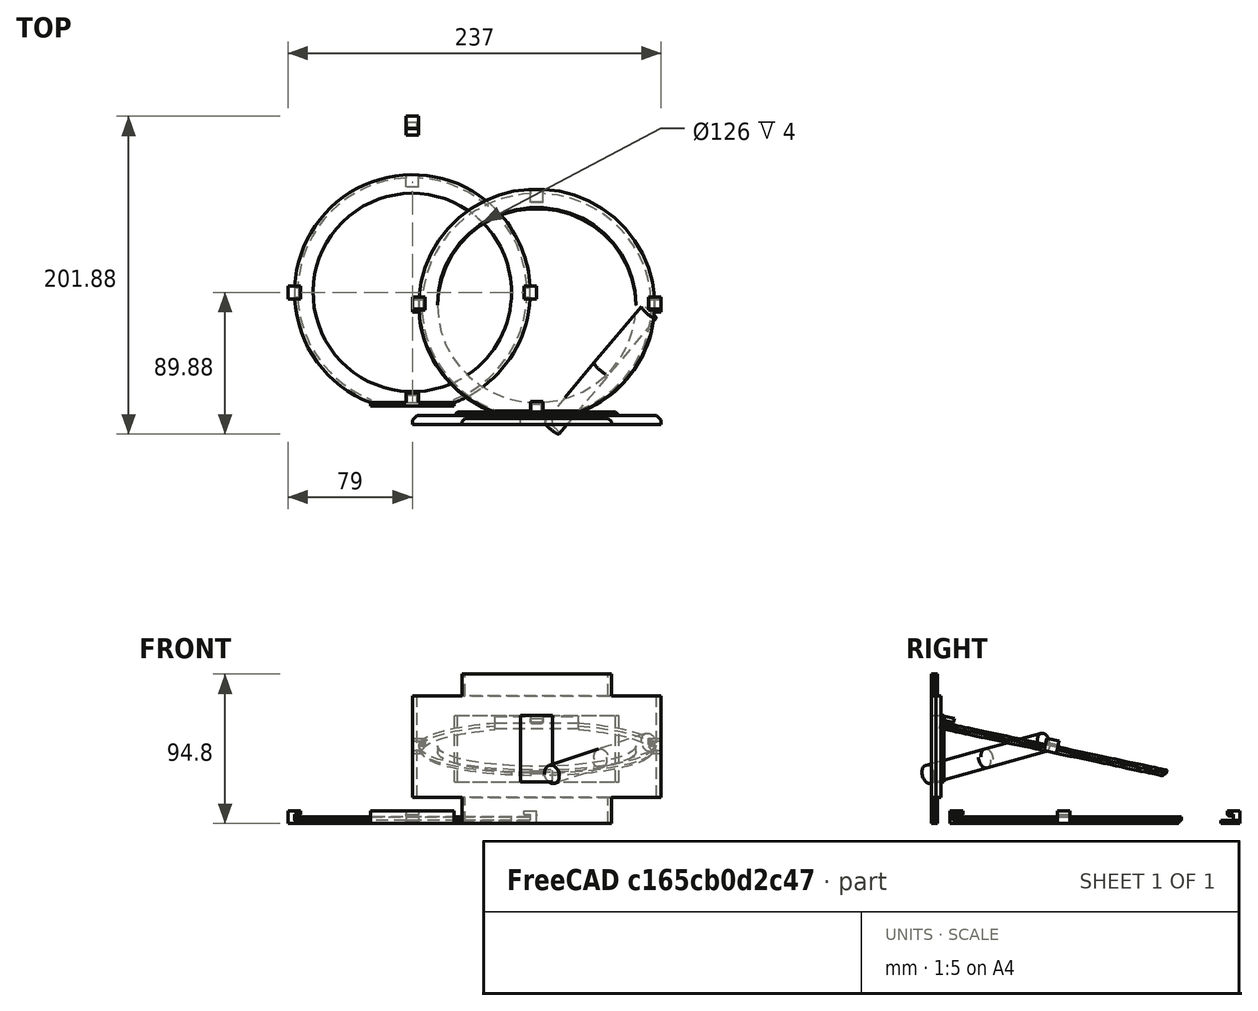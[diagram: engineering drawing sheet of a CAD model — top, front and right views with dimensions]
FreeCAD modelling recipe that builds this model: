
FCSTD DOCUMENT  (FreeCAD 0.19R0.19.2)
Label: waferHolder_016
License: All rights reserved
LicenseURL: http://en.wikipedia.org/wiki/All_rights_reserved
objects: Part::Box×32, Part::Chamfer×28, Part::MultiFuse×12, Part::Cut×10, Part::Cylinder×8, Sketcher::SketchObject×7, Part::Extrusion×7, App::MeasureDistance×1, Part::Fuse×1, Part::Mirroring×1
note: 106 computed .brp shape members not serialized (recipe doc carries the construction recipe); baked Part::Feature solids carry a one-line shape summary decoded from their .brp

FEATURE [Part::Box] Box003  label="bitHolderTop"
  AttacherType = Attacher::AttachEngine3D
  Height = 2
  Length = 8
  Placement = pos=(-4,100,0) rot=(0,0,1;0rad)
  Width = 12
FEATURE [Part::Box] Box008  label="holderBitLeft003"
  AttacherType = Attacher::AttachEngine3D
  Height = 2
  Length = 8
  Placement = pos=(-4,71,2) rot=(0,0,1;0rad)
  Width = 8
FEATURE [Part::Box] Box009  label="bitHolderTopCutout001"
  AttacherType = Attacher::AttachEngine3D
  Height = 4
  Length = 8
  Placement = pos=(-4,67,-2) rot=(0,0,1;0rad)
  Width = 12
FEATURE [Sketcher::SketchObject] Sketch002
  FullyConstrained = true
  sketch-geometry (3):
    g0: Circle CenterX=-3.1415e-12 CenterY=5.6243e-12 CenterZ=0 NormalX=0 NormalY=0 NormalZ=1 AngleXU=0 Radius=63
    g1: ArcOfCircle CenterX=-3.1415e-12 CenterY=5.6243e-12 CenterZ=0 NormalX=0 NormalY=0 NormalZ=1 AngleXU=0 Radius=74.8482 StartAngle=5.07429 EndAngle=10.6337
    g2: LineSegment StartX=-26.5 StartY=-70.0001 StartZ=0 EndX=26.5 EndY=-70.0001 EndZ=0
  constraints (6):
    c: Block(g0)
    c: Coincident(g1,g0)
    c: Block(g1)
    c: Coincident(g2,g1)
    c: Coincident(g2,g1)
    c: Horizontal(g2)
FEATURE [Part::Extrusion] Extrude002  label="mainHolderRing003"
  Base = -> Sketch002
  Dir = (0,0,1)
  DirMode = 2
  FaceMakerClass = Part::FaceMakerBullseye
  LengthFwd = 4
  LengthRev = 0
  Solid = true
  Symmetric = false
FEATURE [Part::Chamfer] Chamfer001
  Base = -> Extrude002
  Edges = 1 edges r=2: [Edge3]
FEATURE [Part::Cut] Cut002  label="mainHolderRing004"
  Base = -> Chamfer001
  Tool = -> Box009
FEATURE [Part::Cut] Cut003  label="bitHolderTop001"
  Base = -> Box008
  Tool = -> Cut002
FEATURE [Part::Box] Box010  label="holderBitLeft004"
  AttacherType = Attacher::AttachEngine3D
  Height = 2
  Length = 8
  Placement = pos=(-4,71,2) rot=(0,0,1;0rad)
  Width = 8
FEATURE [Part::Box] Box011  label="bitHolderTopCutout002"
  AttacherType = Attacher::AttachEngine3D
  Height = 4
  Length = 8
  Placement = pos=(-4,67,-2) rot=(0,0,1;0rad)
  Width = 12
FEATURE [Sketcher::SketchObject] Sketch003
  FullyConstrained = true
  sketch-geometry (3):
    g0: Circle CenterX=-3.1415e-12 CenterY=5.6243e-12 CenterZ=0 NormalX=0 NormalY=0 NormalZ=1 AngleXU=0 Radius=63
    g1: ArcOfCircle CenterX=-3.1415e-12 CenterY=5.6243e-12 CenterZ=0 NormalX=0 NormalY=0 NormalZ=1 AngleXU=0 Radius=74.8482 StartAngle=5.07429 EndAngle=10.6337
    g2: LineSegment StartX=-26.5 StartY=-70.0001 StartZ=0 EndX=26.5 EndY=-70.0001 EndZ=0
  constraints (6):
    c: Block(g0)
    c: Coincident(g1,g0)
    c: Block(g1)
    c: Coincident(g2,g1)
    c: Coincident(g2,g1)
    c: Horizontal(g2)
FEATURE [Part::Extrusion] Extrude003  label="mainHolderRing006"
  Base = -> Sketch003
  Dir = (0,0,1)
  DirMode = 2
  FaceMakerClass = Part::FaceMakerBullseye
  LengthFwd = 4
  LengthRev = 0
  Solid = true
  Symmetric = false
FEATURE [Part::Chamfer] Chamfer002
  Base = -> Extrude003
  Edges = 1 edges r=2: [Edge3]
FEATURE [Part::Cut] Cut005  label="mainHolderRing005"
  Base = -> Chamfer002
  Tool = -> Box011
FEATURE [Part::Cut] Cut004  label="bitHolderTop002"
  Base = -> Box010
  Placement = pos=(0,0,2) rot=(0,0,1;0rad)
  Tool = -> Cut005
FEATURE [Part::Box] Box012  label="holderBitLeft005"
  AttacherType = Attacher::AttachEngine3D
  Height = 2
  Length = 8
  Placement = pos=(-4,71,2) rot=(0,0,1;0rad)
  Width = 8
FEATURE [Part::Box] Box013  label="bitHolderTopCutout003"
  AttacherType = Attacher::AttachEngine3D
  Height = 4
  Length = 8
  Placement = pos=(-4,67,-2) rot=(0,0,1;0rad)
  Width = 12
FEATURE [Sketcher::SketchObject] Sketch004
  FullyConstrained = true
  sketch-geometry (3):
    g0: Circle CenterX=-3.1415e-12 CenterY=5.6243e-12 CenterZ=0 NormalX=0 NormalY=0 NormalZ=1 AngleXU=0 Radius=63
    g1: ArcOfCircle CenterX=-3.1415e-12 CenterY=5.6243e-12 CenterZ=0 NormalX=0 NormalY=0 NormalZ=1 AngleXU=0 Radius=74.8482 StartAngle=5.07429 EndAngle=10.6337
    g2: LineSegment StartX=-26.5 StartY=-70.0001 StartZ=0 EndX=26.5 EndY=-70.0001 EndZ=0
  constraints (6):
    c: Block(g0)
    c: Coincident(g1,g0)
    c: Block(g1)
    c: Coincident(g2,g1)
    c: Coincident(g2,g1)
    c: Horizontal(g2)
FEATURE [Part::Extrusion] Extrude004  label="mainHolderRing008"
  Base = -> Sketch004
  Dir = (0,0,1)
  DirMode = 2
  FaceMakerClass = Part::FaceMakerBullseye
  LengthFwd = 4
  LengthRev = 0
  Solid = true
  Symmetric = false
FEATURE [Part::Chamfer] Chamfer003
  Base = -> Extrude004
  Edges = 1 edges r=2: [Edge3]
FEATURE [Part::Cut] Cut007  label="mainHolderRing007"
  Base = -> Chamfer003
  Tool = -> Box013
FEATURE [Part::Cut] Cut006  label="bitHolderTop003"
  Base = -> Box012
  Placement = pos=(0,0,4) rot=(0,0,1;0rad)
  Tool = -> Cut007
FEATURE [Part::Box] Box014  label="bitHoldertop006"
  AttacherType = Attacher::AttachEngine3D
  Height = 3.4
  Length = 8
  Placement = pos=(-4,71,4.6) rot=(0,0,1;0rad)
  Width = 8
FEATURE [Part::MultiFuse] Fusion001  label="holderTop"
  Placement = pos=(0,33,0) rot=(0,0,1;0rad)
  Shapes = -> [Cut003,Cut004,Cut006,Box014]
FEATURE [Part::Chamfer] Chamfer004
  Base = -> Fusion001
  Edges = 1 edges r=1: [Edge16]
FEATURE [Part::Chamfer] Chamfer009
  Base = -> Chamfer004
  Edges = 1 edges r=1: [Edge1]
FEATURE [Part::Chamfer] Chamfer010
  Base = -> Chamfer009
  Edges = 1 edges r=1: [Edge32]
FEATURE [Part::Box] Box018  label="base001"
  AttacherType = Attacher::AttachEngine3D
  Height = 64.44
  Length = 158
  Placement = pos=(0,-84,16.6) rot=(0,0,1;0rad)
  Width = 6
FEATURE [Part::Box] Box019  label="base002"
  AttacherType = Attacher::AttachEngine3D
  Height = 94.8
  Length = 94.8
  Placement = pos=(31.6,-84,0) rot=(0,0,1;0rad)
  Width = 4
FEATURE [Part::Box] Box020  label="base003"
  AttacherType = Attacher::AttachEngine3D
  Height = 42.44
  Length = 104.28
  Placement = pos=(26.86,-84,26.18) rot=(0,0,1;0rad)
  Width = 8
FEATURE [Part::Chamfer] Chamfer014
  Base = -> Box018
  Edges = 1 edges r=3: [Edge3]
FEATURE [Part::Chamfer] Chamfer015
  Base = -> Chamfer014
  Edges = 1 edges r=3: [Edge15]
FEATURE [Part::Chamfer] Chamfer016
  Base = -> Box019
  Edges = 1 edges r=2: [Edge3]
FEATURE [Part::Chamfer] Chamfer017
  Base = -> Box020
  Edges = 1 edges r=2: [Edge3]
FEATURE [Part::Chamfer] Chamfer018
  Base = -> Chamfer016
  Edges = 1 edges r=2: [Edge15]
FEATURE [Part::Chamfer] Chamfer019
  Base = -> Chamfer017
  Edges = 1 edges r=2: [Edge15]
FEATURE [Part::MultiFuse] Fusion002  label="base004"
  Shapes = -> [Chamfer015,Chamfer018,Chamfer019]
FEATURE [Part::Box] Box021  label="holderBitLeft006"
  AttacherType = Attacher::AttachEngine3D
  Height = 4
  Length = 6
  Placement = pos=(-79,-4,0) rot=(0,0,1;0rad)
  Width = 8
FEATURE [Part::Box] Box022  label="holderBitright003"
  AttacherType = Attacher::AttachEngine3D
  Height = 4
  Length = 6
  Placement = pos=(73,-4,0) rot=(0,0,1;0rad)
  Width = 8
FEATURE [Part::Box] Box023  label="holderBitLeft007"
  AttacherType = Attacher::AttachEngine3D
  Height = 3.4
  Length = 8
  Placement = pos=(-79,-4,4.6) rot=(0,0,1;0rad)
  Width = 8
FEATURE [Part::Box] Box024  label="holderBitRight003"
  AttacherType = Attacher::AttachEngine3D
  Height = 3.4
  Length = 8
  Placement = pos=(71,-4,4.6) rot=(0,0,1;0rad)
  Width = 8
FEATURE [Sketcher::SketchObject] Sketch005
  FullyConstrained = true
  sketch-geometry (3):
    g0: Circle CenterX=-3.1415e-12 CenterY=5.6243e-12 CenterZ=0 NormalX=0 NormalY=0 NormalZ=1 AngleXU=0 Radius=63
    g1: ArcOfCircle CenterX=-3.1415e-12 CenterY=5.6243e-12 CenterZ=0 NormalX=0 NormalY=0 NormalZ=1 AngleXU=0 Radius=74.8482 StartAngle=5.07429 EndAngle=10.6337
    g2: LineSegment StartX=-26.5 StartY=-70.0001 StartZ=0 EndX=26.5 EndY=-70.0001 EndZ=0
  constraints (6):
    c: Block(g0)
    c: Coincident(g1,g0)
    c: Block(g1)
    c: Coincident(g2,g1)
    c: Coincident(g2,g1)
    c: Horizontal(g2)
FEATURE [Part::Box] Box025  label="holderBitLeft008"
  AttacherType = Attacher::AttachEngine3D
  Height = 4
  Length = 8
  Placement = pos=(-79,-4,0) rot=(0,0,1;0rad)
  Width = 8
FEATURE [Part::Box] Box026  label="bitHolderTopCutout004"
  AttacherType = Attacher::AttachEngine3D
  Height = 4
  Length = 8
  Placement = pos=(-4,67,-2) rot=(0,0,1;0rad)
  Width = 12
FEATURE [Part::Extrusion] Extrude006  label="mainHolderRing010"
  Base = -> Sketch005
  Dir = (0,0,1)
  DirMode = 2
  FaceMakerClass = Part::FaceMakerBullseye
  LengthFwd = 4
  LengthRev = 0
  Solid = true
  Symmetric = false
FEATURE [Part::Box] Box027  label="holderBitRight004"
  AttacherType = Attacher::AttachEngine3D
  Height = 4
  Length = 8
  Placement = pos=(71,-4,0) rot=(0,0,1;0rad)
  Width = 8
FEATURE [Part::Chamfer] Chamfer020
  Base = -> Extrude006
  Edges = 1 edges r=2: [Edge3]
FEATURE [Part::Cut] Cut008  label="mainHolderRing011"
  Base = -> Chamfer020
  Tool = -> Box026
FEATURE [Part::MultiFuse] Fusion004  label="holders001"
  Shapes = -> [Box021,Box022]
FEATURE [Sketcher::SketchObject] Sketch006
  FullyConstrained = true
  sketch-geometry (3):
    g0: Circle CenterX=-3.1415e-12 CenterY=5.6243e-12 CenterZ=0 NormalX=0 NormalY=0 NormalZ=1 AngleXU=0 Radius=63
    g1: ArcOfCircle CenterX=-3.1415e-12 CenterY=5.6243e-12 CenterZ=0 NormalX=0 NormalY=0 NormalZ=1 AngleXU=0 Radius=74.8482 StartAngle=5.07429 EndAngle=10.6337
    g2: LineSegment StartX=-26.5 StartY=-70.0001 StartZ=0 EndX=26.5 EndY=-70.0001 EndZ=0
  constraints (6):
    c: Block(g0)
    c: Coincident(g1,g0)
    c: Block(g1)
    c: Coincident(g2,g1)
    c: Coincident(g2,g1)
    c: Horizontal(g2)
FEATURE [Part::Extrusion] Extrude005  label="mainHolderRing009"
  Base = -> Sketch006
  Dir = (0,0,1)
  DirMode = 2
  FaceMakerClass = Part::FaceMakerBullseye
  LengthFwd = 4
  LengthRev = 0
  Solid = true
  Symmetric = false
FEATURE [Part::Cut] Cut009  label="leftAndRightHolderBits001"
  Base = -> Fusion004
  Placement = pos=(0,0,4) rot=(0,0,1;0rad)
  Tool = -> Extrude005
FEATURE [Part::Chamfer] Chamfer021
  Base = -> Box023
  Edges = 1 edges r=1: [Edge8]
FEATURE [Part::Chamfer] Chamfer022
  Base = -> Box024
  Edges = 1 edges r=1: [Edge4]
FEATURE [Part::Chamfer] Chamfer023
  Base = -> Chamfer022
  Edges = 1 edges r=1: [Edge13]
FEATURE [Part::Chamfer] Chamfer024
  Base = -> Chamfer023
  Edges = 1 edges r=1: [Edge5]
FEATURE [Part::Box] Box028  label="holderBottom004"
  AttacherType = Attacher::AttachEngine3D
  Height = 4
  Length = 53
  Placement = pos=(-26.5,-72,0) rot=(0,0,1;0rad)
  Width = 4.5
FEATURE [Part::Chamfer] Chamfer025
  Base = -> Chamfer021
  Edges = 1 edges r=1: [Edge5]
FEATURE [Part::Chamfer] Chamfer026
  Base = -> Chamfer025
  Edges = 1 edges r=1: [Edge16]
FEATURE [Part::Box] Box029  label="holderBottom006"
  AttacherType = Attacher::AttachEngine3D
  Height = 4
  Length = 53
  Placement = pos=(-26.5,-72,4) rot=(0,0,1;0rad)
  Width = 2
FEATURE [Part::Box] Box030  label="holderBottom007"
  AttacherType = Attacher::AttachEngine3D
  Height = 3.4
  Length = 8
  Placement = pos=(-4,-72,4.6) rot=(0,0,1;0rad)
  Width = 8
FEATURE [Part::Chamfer] Chamfer027  label="holderBottom005"
  Base = -> Box030
  Edges = 3 edges r=1: [Edge4,Edge8,Edge11]
FEATURE [Part::MultiFuse] Fusion005  label="ringHolder001"
  Placement = pos=(79,-8.35,45.4) rot=(1,0,0;6.07375rad)
  Shapes = -> [Box025,Box027,Cut008,Cut009,Chamfer024,Chamfer026,Box028,Box029,Chamfer027]
FEATURE [Part::Box] Box017  label="holderBottom002"
  AttacherType = Attacher::AttachEngine3D
  Height = 3.4
  Length = 8
  Placement = pos=(-4,-72,4.6) rot=(0,0,1;0rad)
  Width = 8
FEATURE [Part::Chamfer] Chamfer013  label="holderBottom003"
  Base = -> Box017
  Edges = 3 edges r=1: [Edge4,Edge8,Edge11]
FEATURE [Part::Box] Box016  label="holderBottom001"
  AttacherType = Attacher::AttachEngine3D
  Height = 4
  Length = 53
  Placement = pos=(-26.5,-72,4) rot=(0,0,1;0rad)
  Width = 2
FEATURE [Part::Box] Box015  label="holderBottom"
  AttacherType = Attacher::AttachEngine3D
  Height = 4
  Length = 53
  Placement = pos=(-26.5,-72,0) rot=(0,0,1;0rad)
  Width = 4.5
FEATURE [Part::Box] Box006  label="holderBitLeft002"
  AttacherType = Attacher::AttachEngine3D
  Height = 3.4
  Length = 8
  Placement = pos=(-79,-4,4.6) rot=(0,0,1;0rad)
  Width = 8
FEATURE [Part::Chamfer] Chamfer005
  Base = -> Box006
  Edges = 1 edges r=1: [Edge8]
FEATURE [Part::Chamfer] Chamfer011
  Base = -> Chamfer005
  Edges = 1 edges r=1: [Edge5]
FEATURE [Part::Chamfer] Chamfer012
  Base = -> Chamfer011
  Edges = 1 edges r=1: [Edge16]
FEATURE [Part::Box] Box007  label="holderBitRight002"
  AttacherType = Attacher::AttachEngine3D
  Height = 3.4
  Length = 8
  Placement = pos=(71,-4,4.6) rot=(0,0,1;0rad)
  Width = 8
FEATURE [Part::Chamfer] Chamfer006
  Base = -> Box007
  Edges = 1 edges r=1: [Edge4]
FEATURE [Part::Chamfer] Chamfer007
  Base = -> Chamfer006
  Edges = 1 edges r=1: [Edge13]
FEATURE [Part::Chamfer] Chamfer008
  Base = -> Chamfer007
  Edges = 1 edges r=1: [Edge5]
FEATURE [Sketcher::SketchObject] Sketch001
  FullyConstrained = true
  sketch-geometry (3):
    g0: Circle CenterX=-3.1415e-12 CenterY=5.6243e-12 CenterZ=0 NormalX=0 NormalY=0 NormalZ=1 AngleXU=0 Radius=63
    g1: ArcOfCircle CenterX=-3.1415e-12 CenterY=5.6243e-12 CenterZ=0 NormalX=0 NormalY=0 NormalZ=1 AngleXU=0 Radius=74.8482 StartAngle=5.07429 EndAngle=10.6337
    g2: LineSegment StartX=-26.5 StartY=-70.0001 StartZ=0 EndX=26.5 EndY=-70.0001 EndZ=0
  constraints (6):
    c: Block(g0)
    c: Coincident(g1,g0)
    c: Block(g1)
    c: Coincident(g2,g1)
    c: Coincident(g2,g1)
    c: Horizontal(g2)
FEATURE [Part::Extrusion] Extrude001  label="mainHolderRing002"
  Base = -> Sketch001
  Dir = (0,0,1)
  DirMode = 2
  FaceMakerClass = Part::FaceMakerBullseye
  LengthFwd = 4
  LengthRev = 0
  Solid = true
  Symmetric = false
FEATURE [Part::Box] Box005  label="holderBitright002"
  AttacherType = Attacher::AttachEngine3D
  Height = 4
  Length = 6
  Placement = pos=(73,-4,0) rot=(0,0,1;0rad)
  Width = 8
FEATURE [Part::Box] Box004  label="holderBitLeft001"
  AttacherType = Attacher::AttachEngine3D
  Height = 4
  Length = 6
  Placement = pos=(-79,-4,0) rot=(0,0,1;0rad)
  Width = 8
FEATURE [Part::MultiFuse] Fusion  label="holders"
  Shapes = -> [Box004,Box005]
FEATURE [Part::Cut] Cut001  label="leftAndRightHolderBits"
  Base = -> Fusion
  Placement = pos=(0,0,4) rot=(0,0,1;0rad)
  Tool = -> Extrude001
FEATURE [Part::Box] Box001  label="bitHolderTopCutout"
  AttacherType = Attacher::AttachEngine3D
  Height = 4
  Length = 8
  Placement = pos=(-4,67,-2) rot=(0,0,1;0rad)
  Width = 12
FEATURE [Sketcher::SketchObject] Sketch
  FullyConstrained = true
  sketch-geometry (3):
    g0: Circle CenterX=-3.1415e-12 CenterY=5.6243e-12 CenterZ=0 NormalX=0 NormalY=0 NormalZ=1 AngleXU=0 Radius=63
    g1: ArcOfCircle CenterX=-3.1415e-12 CenterY=5.6243e-12 CenterZ=0 NormalX=0 NormalY=0 NormalZ=1 AngleXU=0 Radius=74.8482 StartAngle=5.07429 EndAngle=10.6337
    g2: LineSegment StartX=-26.5 StartY=-70.0001 StartZ=0 EndX=26.5 EndY=-70.0001 EndZ=0
  constraints (6):
    c: Block(g0)
    c: Coincident(g1,g0)
    c: Block(g1)
    c: Coincident(g2,g1)
    c: Coincident(g2,g1)
    c: Horizontal(g2)
FEATURE [Part::Extrusion] Extrude  label="mainHolderRing"
  Base = -> Sketch
  Dir = (0,0,1)
  DirMode = 2
  FaceMakerClass = Part::FaceMakerBullseye
  LengthFwd = 4
  LengthRev = 0
  Solid = true
  Symmetric = false
FEATURE [Part::Chamfer] Chamfer
  Base = -> Extrude
  Edges = 1 edges r=2: [Edge3]
FEATURE [Part::Cut] Cut  label="mainHolderRing001"
  Base = -> Chamfer
  Tool = -> Box001
FEATURE [Part::Box] Box002  label="holderBitRight"
  AttacherType = Attacher::AttachEngine3D
  Height = 4
  Length = 8
  Placement = pos=(71,-4,0) rot=(0,0,1;0rad)
  Width = 8
FEATURE [Part::Box] Box  label="holderBitLeft"
  AttacherType = Attacher::AttachEngine3D
  Height = 4
  Length = 8
  Placement = pos=(-79,-4,0) rot=(0,0,1;0rad)
  Width = 8
FEATURE [Part::MultiFuse] Fusion003  label="ringHolder"
  Shapes = -> [Box,Box002,Cut,Cut001,Chamfer008,Chamfer012,Box015,Box016,Chamfer013]
FEATURE [Part::Cylinder] Cylinder
  Angle = 360
  AttacherType = Attacher::AttachEngine3D
  Height = 50
  Placement = pos=(34.86,-30,47.4) rot=(1,0,0;1.5708rad)
  Radius = 6
FEATURE [Part::Box] Box031  label="base005"
  AttacherType = Attacher::AttachEngine3D
  Height = 42.44
  Length = 20.28
  Placement = pos=(68.86,-84,26.18) rot=(0,0,1;0rad)
  Width = 8
FEATURE [Part::Cylinder] Cylinder001
  Angle = 360
  AttacherType = Attacher::AttachEngine3D
  Height = 50
  Placement = pos=(34.86,-30,47.4) rot=(1,0,0;1.5708rad)
  Radius = 6
FEATURE [Part::MultiFuse] Fusion006
  Placement = pos=(0,0,0) rot=(1,0,0;0.20944rad)
  Shapes = -> [Cylinder001,Cylinder]
FEATURE [Part::Cylinder] Cylinder002
  Angle = 360
  AttacherType = Attacher::AttachEngine3D
  Height = 50
  Placement = pos=(34.86,-30,47.4) rot=(1,0,0;1.5708rad)
  Radius = 6
FEATURE [Part::Cylinder] Cylinder003
  Angle = 360
  AttacherType = Attacher::AttachEngine3D
  Height = 50
  Placement = pos=(34.86,-30,47.4) rot=(1,0,0;1.5708rad)
  Radius = 6
FEATURE [Part::MultiFuse] Fusion007
  Placement = pos=(0,0,0) rot=(1,0,0;0.20944rad)
  Shapes = -> [Cylinder003,Cylinder002]
FEATURE [Part::MultiFuse] Fusion008
  Placement = pos=(-44.06,-5,11.27) rot=(0,0,1;0.698132rad)
  Shapes = -> [Fusion007,Fusion006]
FEATURE [App::MeasureDistance] Distance  label="Distance: 0.65 mm"
  Distance = 0.654413
  P1 = (68.86,-76,67.959)
  P2 = (68.8586,-76,68.6134)
FEATURE [Part::Cylinder] Cylinder004
  Angle = 360
  AttacherType = Attacher::AttachEngine3D
  Height = 50
  Placement = pos=(34.86,-30,47.4) rot=(1,0,0;1.5708rad)
  Radius = 6
FEATURE [Part::Cylinder] Cylinder005
  Angle = 360
  AttacherType = Attacher::AttachEngine3D
  Height = 50
  Placement = pos=(34.86,-30,47.4) rot=(1,0,0;1.5708rad)
  Radius = 6
FEATURE [Part::MultiFuse] Fusion010
  Placement = pos=(0,0,0) rot=(1,0,0;0.20944rad)
  Shapes = -> [Cylinder005,Cylinder004]
FEATURE [Part::Cylinder] Cylinder006
  Angle = 360
  AttacherType = Attacher::AttachEngine3D
  Height = 50
  Placement = pos=(34.86,-30,47.4) rot=(1,0,0;1.5708rad)
  Radius = 6
FEATURE [Part::Cylinder] Cylinder007
  Angle = 360
  AttacherType = Attacher::AttachEngine3D
  Height = 50
  Placement = pos=(34.86,-30,47.4) rot=(1,0,0;1.5708rad)
  Radius = 6
FEATURE [Part::MultiFuse] Fusion009
  Placement = pos=(0,0,0) rot=(1,0,0;0.20944rad)
  Shapes = -> [Cylinder007,Cylinder006]
FEATURE [Part::MultiFuse] Fusion011
  Placement = pos=(-14,-40.82,1.35) rot=(0,0,1;0.698132rad)
  Shapes = -> [Fusion009,Fusion010]
FEATURE [Part::Fuse] Fusion012
  Base = -> Fusion008
  Tool = -> Fusion011
FEATURE [Part::Mirroring] Part__Mirroring  label="Fusion012 (Mirror #1)"
  Base = (0,0,0)
  Normal = (1,0,0)
  Placement = pos=(158,0,0) rot=(0,0,1;0rad)
  Source = -> Fusion012
